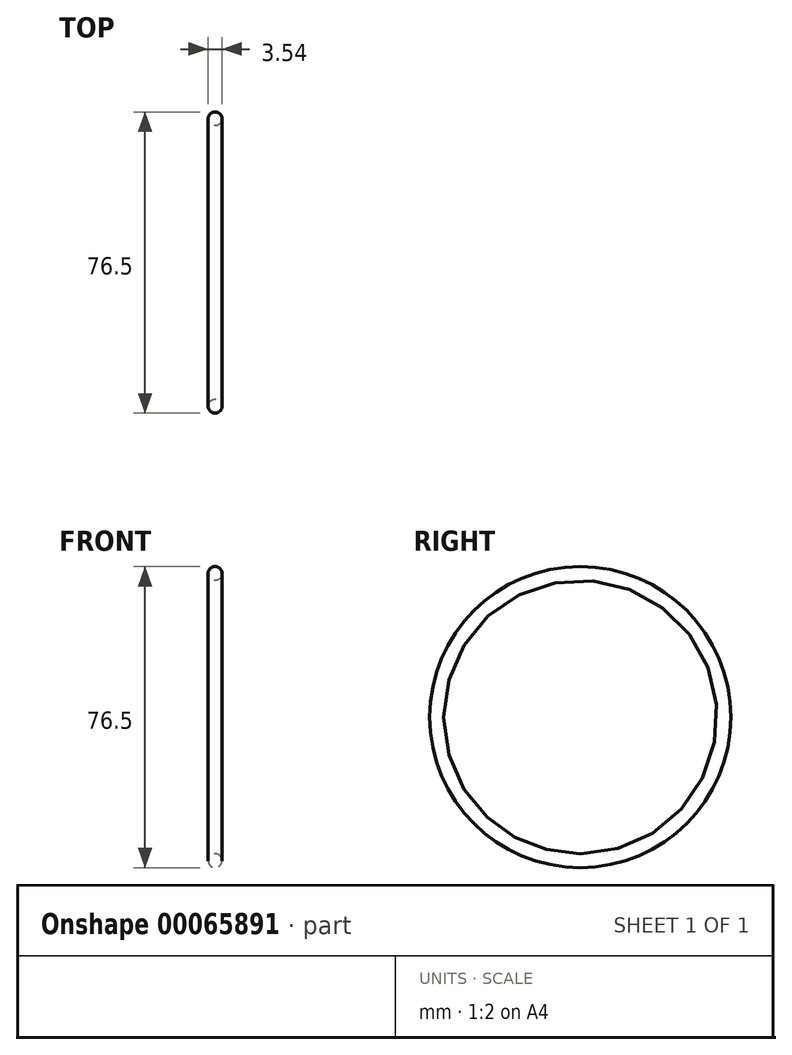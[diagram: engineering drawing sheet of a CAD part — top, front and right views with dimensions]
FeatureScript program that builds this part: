
annotation { "Feature Type Name" : "Feature", "Feature Type Description" : "" }
export const myFeature = defineFeature(function(context is Context, id is Id, definition is map)
    precondition{}
    {
        {
            var Q0;
            Q0=qCreatedBy(makeId("Front.planeOp"),FACE);
            var sketch = newSketch(context, id + "F0", { "sketchPlane" : qUnion([Q0])});
            skLineSegment(sketch, "E0", {"start": v(0, 0) * mm, "end": v(-6.06, 0) * mm, "construction": true});
            skCircle(sketch, "E1", {"center": v(0, 36.49) * mm, "radius": 1.77 * mm});
            skSolve(sketch);
        }
        {
            var Q0;
            Q0=makeQuery(id+"F0.imprint","IMPRINT",FACE,{"disambiguationData":[TD([[makeQuery(id+"F0.imprint","IMPRINT",EDGE,{"derivedFrom":sQuery(id+"F0.wireOp",EDGE,"E1")}),1.0]])]});
            var Q1;
            Q1=sQuery(id+"F0.wireOp",EDGE,"E0");
            revolve(context, id + "F1", {"entities" : qUnion([Q0]), "axis" : qUnion([Q1]), "revolveType" : RevolveType.FULL});
        }
    });
